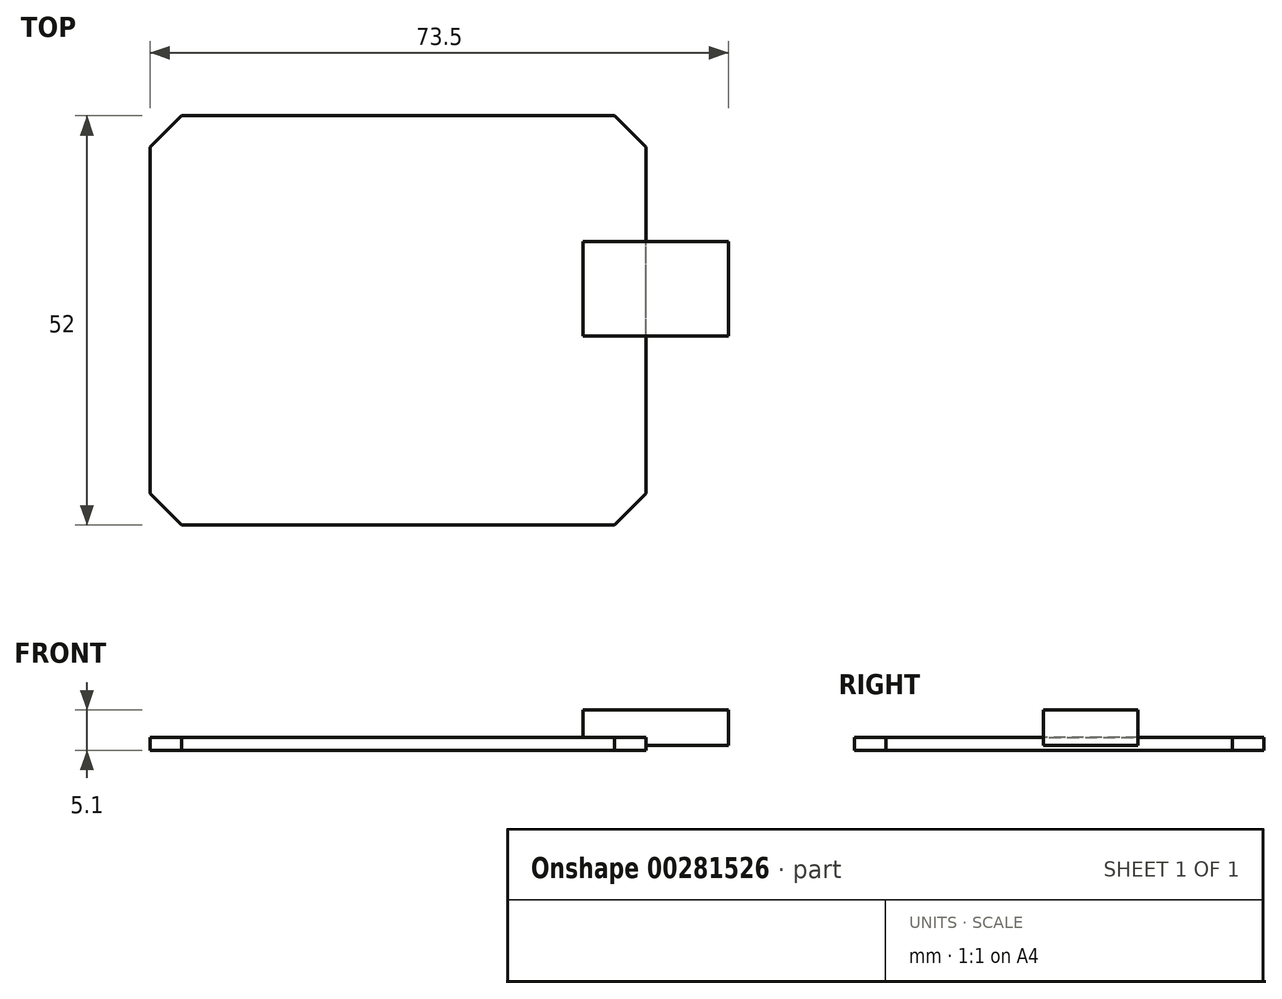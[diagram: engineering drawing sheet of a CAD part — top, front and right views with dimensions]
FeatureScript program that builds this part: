
annotation { "Feature Type Name" : "Feature", "Feature Type Description" : "" }
export const myFeature = defineFeature(function(context is Context, id is Id, definition is map)
    precondition{}
    {
        {
            var Q0;
            Q0=qCreatedBy(makeId("Top.planeOp"),FACE);
            var sketch = newSketch(context, id + "F0", { "sketchPlane" : qUnion([Q0])});
            skLineSegment(sketch, "E0.bottom", {"start": v(0, 0) * mm, "end": v(-63, 0) * mm});
            skLineSegment(sketch, "E0.top", {"start": v(0, 52) * mm, "end": v(-63, 52) * mm});
            skLineSegment(sketch, "E0.left", {"start": v(0, 0) * mm, "end": v(0, 52) * mm});
            skLineSegment(sketch, "E0.right", {"start": v(-63, 0) * mm, "end": v(-63, 52) * mm});
            skPoint(sketch, "E1.visualSharp", {"position": v(-63, 52) * mm});
            skPoint(sketch, "E2.visualSharp", {"position": v(0, 52) * mm});
            skPoint(sketch, "E3.visualSharp", {"position": v(-63, 0) * mm});
            skPoint(sketch, "E4.visualSharp", {"position": v(0, 0) * mm});
            skSolve(sketch);
        }
        {
            var Q0;
            Q0 = qSketchRegion(id + "F0", true);
            extrude(context, id + "F1", {"entities" : qUnion([Q0]), "depth" : 1.6 * mm});
        }
        {
            var Q0;
            Q0=makeQuery(id+"F1.opExtrude","CAP_FACE",FACE,{"disambiguationData":[OSD([sQuery(id+"F0.wireOp",EDGE,"E0.bottom"),sQuery(id+"F0.wireOp",EDGE,"E0.top"),sQuery(id+"F0.wireOp",EDGE,"E0.left"),sQuery(id+"F0.wireOp",EDGE,"E0.right"),sQuery(id+"F0.wireOp",EDGE,"E1.filletArc"),sQuery(id+"F0.wireOp",EDGE,"E2.filletArc"),sQuery(id+"F0.wireOp",EDGE,"E3.filletArc"),sQuery(id+"F0.wireOp",EDGE,"E4.filletArc")])],"isStart":false});
            var sketch = newSketch(context, id + "F2", { "sketchPlane" : qUnion([Q0])});
            skLineSegment(sketch, "E5.bottom", {"start": v(-8, 36) * mm, "end": v(10.5, 36) * mm});
            skLineSegment(sketch, "E5.top", {"start": v(-8, 24) * mm, "end": v(10.5, 24) * mm});
            skLineSegment(sketch, "E5.left", {"start": v(-8, 36) * mm, "end": v(-8, 24) * mm});
            skLineSegment(sketch, "E5.right", {"start": v(10.5, 36) * mm, "end": v(10.5, 24) * mm});
            skSolve(sketch);
        }
        {
            var Q0;
            Q0 = qSketchRegion(id + "F2", true);
            extrude(context, id + "F3", {"entities" : qUnion([Q0]), "operationType" : NewBodyOperationType.ADD, "depth" : 3.5 * mm});
        }
        {
            var Q0;
            Q0=makeQuery(id+"F3.opExtrude","CAP_FACE",FACE,{"disambiguationData":[OSD([sQuery(id+"F2.wireOp",EDGE,"E5.bottom"),sQuery(id+"F2.wireOp",EDGE,"E5.top"),sQuery(id+"F2.wireOp",EDGE,"E5.left"),sQuery(id+"F2.wireOp",EDGE,"E5.right")])],"isStart":true});
            var sketch = newSketch(context, id + "F4", { "sketchPlane" : qUnion([Q0])});
            skLineSegment(sketch, "E6.bottom", {"start": v(0, -24) * mm, "end": v(10.5, -24) * mm});
            skLineSegment(sketch, "E6.top", {"start": v(0, -36) * mm, "end": v(10.5, -36) * mm});
            skLineSegment(sketch, "E6.left", {"start": v(0, -24) * mm, "end": v(0, -36) * mm});
            skLineSegment(sketch, "E6.right", {"start": v(10.5, -24) * mm, "end": v(10.5, -36) * mm});
            skSolve(sketch);
        }
        {
            var Q0;
            Q0=makeQuery(id+"F4.imprint","IMPRINT",FACE,{"disambiguationData":[TD([[makeQuery(id+"F4.imprint","IMPRINT",EDGE,{"derivedFrom":sQuery(id+"F4.wireOp",EDGE,"E6.bottom")}),-1.0]])]});
            extrude(context, id + "F5", {"entities" : qUnion([Q0]), "operationType" : NewBodyOperationType.ADD, "depth" : 1 * mm});
        }
        {
            var Q0;
            Q0=makeQuery(id+"F1.opExtrude","SWEPT_EDGE",EDGE,{"disambiguationData":[OSD([sQuery(id+"F0.wireOp",EDGE,"E0.top"),sQuery(id+"F0.wireOp",EDGE,"E0.right")])]});
            var Q1;
            Q1=makeQuery(id+"F1.opExtrude","SWEPT_EDGE",EDGE,{"disambiguationData":[OSD([sQuery(id+"F0.wireOp",EDGE,"E0.top"),sQuery(id+"F0.wireOp",EDGE,"E0.left")])]});
            var Q2;
            Q2=makeQuery(id+"F1.opExtrude","SWEPT_EDGE",EDGE,{"disambiguationData":[OSD([sQuery(id+"F0.wireOp",EDGE,"E0.bottom"),sQuery(id+"F0.wireOp",EDGE,"E0.right")])]});
            var Q3;
            Q3=makeQuery(id+"F1.opExtrude","SWEPT_EDGE",EDGE,{"disambiguationData":[OSD([sQuery(id+"F0.wireOp",EDGE,"E0.bottom"),sQuery(id+"F0.wireOp",EDGE,"E0.left")])]});
            chamfer(context, id + "F6", {"entities" : qUnion([Q0, Q1, Q2, Q3]), "width" : 4 * mm, "tangentPropagation" : true});
        }
    });
